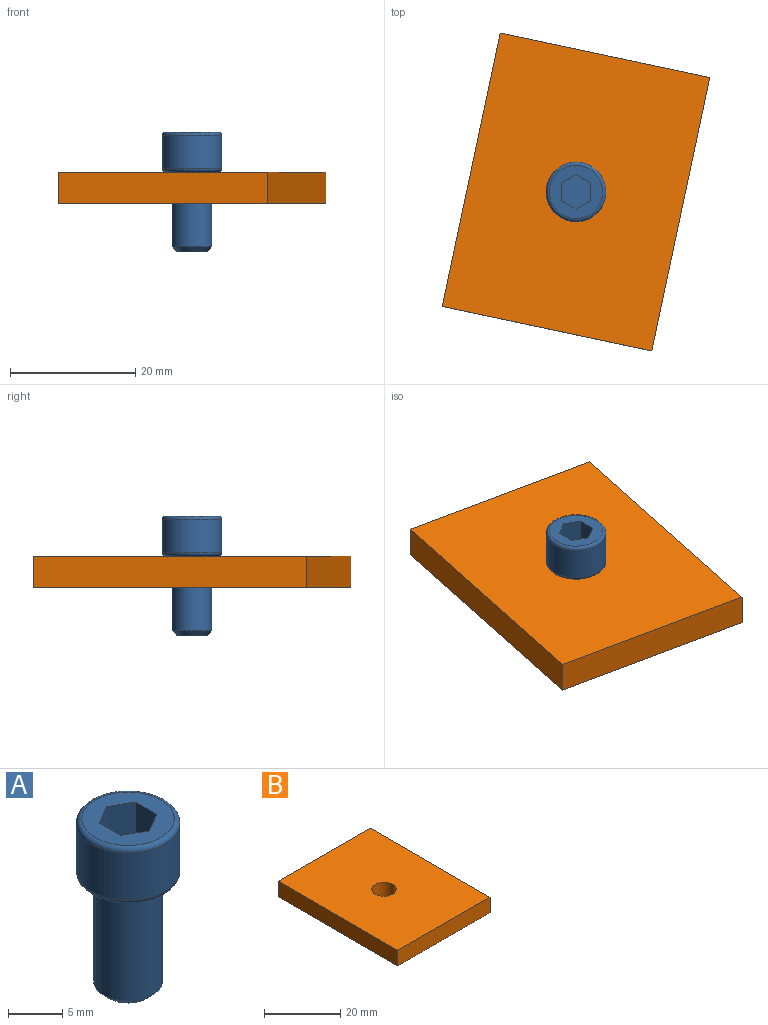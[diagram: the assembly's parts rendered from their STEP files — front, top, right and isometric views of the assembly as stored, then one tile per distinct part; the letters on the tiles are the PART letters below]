
ASSEMBLY  parts=2 mates=1
PART A: 15 faces, bbox 10.3x10.3x19.1 mm
  f0: plane 8.51x8.51mm, normal (0,0,1), area 37.2mm2, adj f5,f6,f7,f8,f9,f10,f14
  f1: cylinder r=3.17mm len=11.94mm, axis (0,0,1), area 238.2mm2, adj f4,f12
  f2: plane 4.83x4.83mm, normal (0,0,-1), area 18.3mm2, adj f12
  f3: cylinder r=4.76mm len=9.53mm, axis (0,0,-1), area 159.6mm2, adj f13,f14
  f4: plane 8.51x8.51mm, normal (0,0,-1), area 25.2mm2, adj f1,f13
  f5: plane 4.83x2.38mm, normal (-0.5,-0.87,0), area 13.3mm2, adj f0,f6,f10,f11
  f6: plane 4.83x2.38mm, normal (0.5,-0.87,0), area 13.3mm2, adj f0,f5,f7,f11
  f7: plane 4.83x2.75mm, normal (1,0,0), area 13.3mm2, adj f0,f6,f8,f11
  f8: plane 4.83x2.38mm, normal (0.5,0.87,0), area 13.3mm2, adj f0,f7,f9,f11
  f9: plane 4.83x2.38mm, normal (-0.5,0.87,0), area 13.3mm2, adj f0,f8,f10,f11
  f10: plane 4.83x2.75mm, normal (-1,0,0), area 13.3mm2, adj f0,f5,f9,f11
  f11: plane 5.5x4.76mm, normal (0,0,1), area 19.6mm2, adj f5,f6,f7,f8,f9,f10
  f12: cone r=3.17mm half-angle=45deg, axis (0,0,1), area 18.9mm2, adj f1,f2
  f13: torus R=4.25mm, axis (0,0,1), area 23mm2, adj f3,f4
  f14: torus R=4.25mm, axis (0,0,1), area 23mm2, adj f0,f3
PART B: 7 faces, bbox 34.2x44.6x5 mm
  f0: plane 44.6x5mm, normal (-1,0,0), area 223mm2, adj f1,f3,f5,f6
  f1: plane 34.2x5mm, normal (0,-1,0), area 171mm2, adj f0,f2,f5,f6
  f2: plane 44.6x5mm, normal (1,0,0), area 223mm2, adj f1,f3,f5,f6
  f3: plane 34.2x5mm, normal (0,1,0), area 171mm2, adj f0,f2,f5,f6
  f4: cylinder r=3.2mm len=6.4mm, axis (0,0,-1), area 100.5mm2, adj f5,f6
  f5: plane 44.6x34.2mm, normal (0,0,1), area 1493.2mm2, adj f0,f1,f2,f3,f4
  f6: plane 44.6x34.2mm, normal (0,0,-1), area 1493.2mm2, adj f0,f1,f2,f3,f4
PLACE A at identity fixed
PLACE B rot(axis=(0,0,-1),12deg) t=(24.15,-6.25,-5)mm
MATE revolute A.f1 <-> B.f4  axis (0,0,1) through (0,0,0)mm
